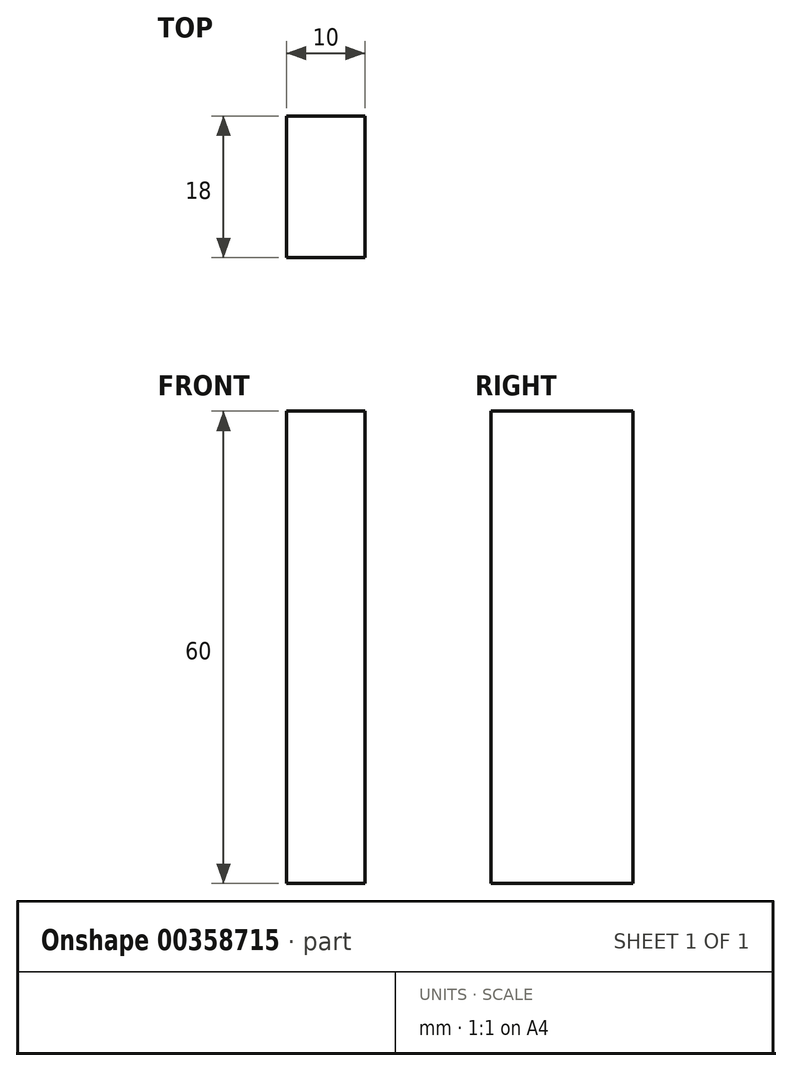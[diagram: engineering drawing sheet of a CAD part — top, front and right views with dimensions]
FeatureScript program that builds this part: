
annotation { "Feature Type Name" : "Feature", "Feature Type Description" : "" }
export const myFeature = defineFeature(function(context is Context, id is Id, definition is map)
    precondition{}
    {
        {
            var Q0;
            Q0=qCreatedBy(makeId("Right.planeOp"),FACE);
            var sketch = newSketch(context, id + "F0", { "sketchPlane" : qUnion([Q0])});
            skLineSegment(sketch, "E0.bottom", {"start": v(9, -30) * mm, "end": v(-9, -30) * mm});
            skLineSegment(sketch, "E0.top", {"start": v(9, 30) * mm, "end": v(-9, 30) * mm});
            skLineSegment(sketch, "E0.left", {"start": v(9, -30) * mm, "end": v(9, 30) * mm});
            skLineSegment(sketch, "E0.right", {"start": v(-9, -30) * mm, "end": v(-9, 30) * mm});
            skPoint(sketch, "E0.middle", {"position": v(0, 0) * mm});
            skSolve(sketch);
        }
        {
            var Q0;
            Q0 = qSketchRegion(id + "F0", true);
            extrude(context, id + "F1", {"entities" : qUnion([Q0]), "endBound" : BoundingType.SYMMETRIC, "depth" : 10 * mm});
        }
    });
